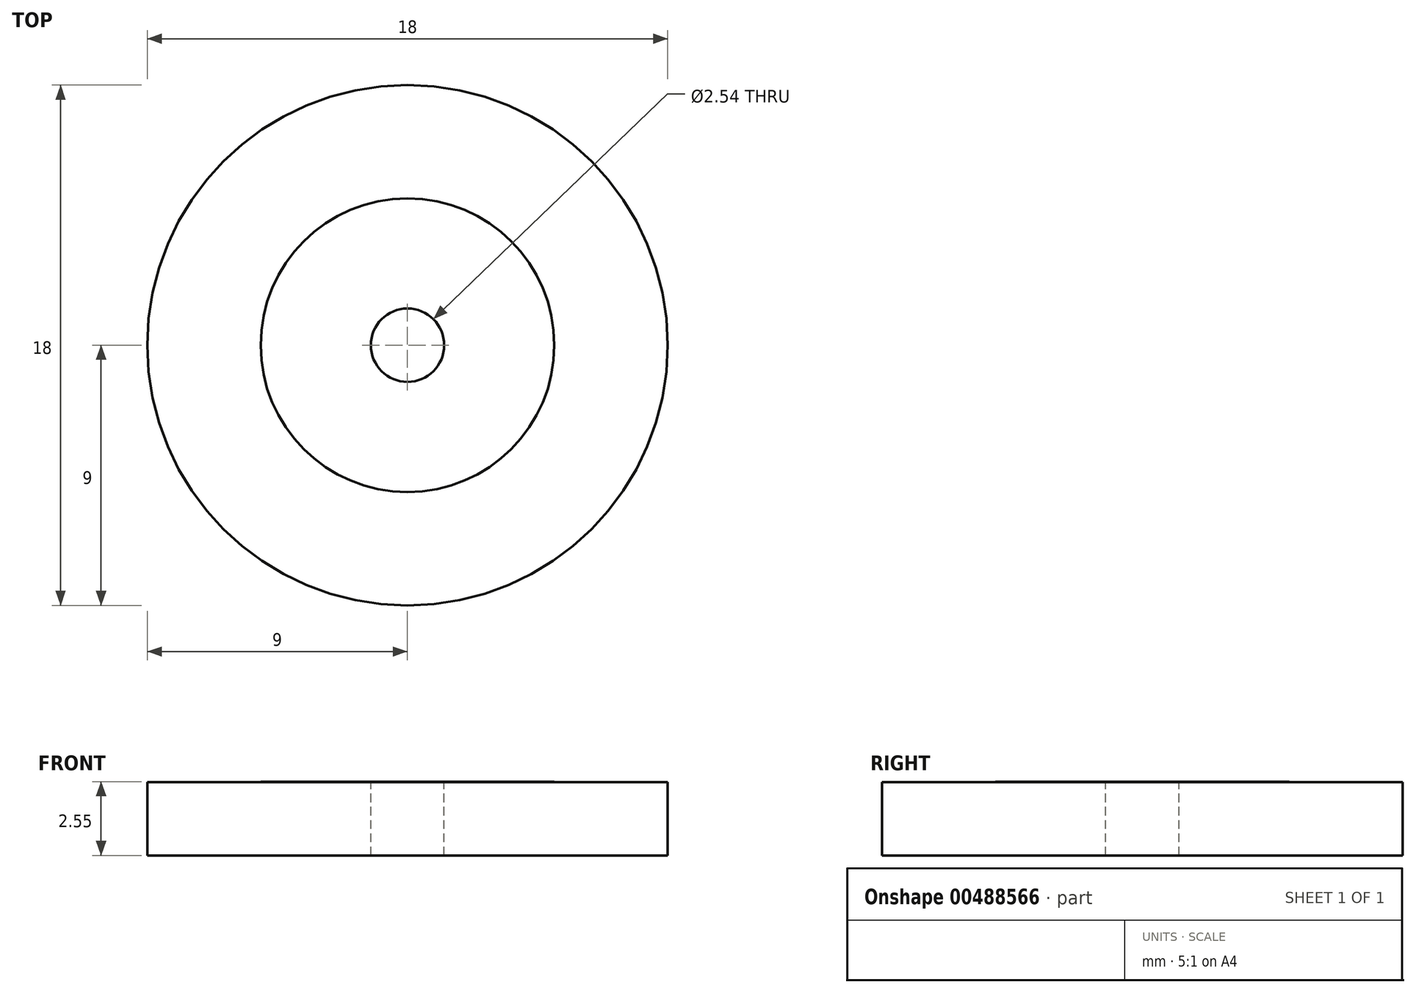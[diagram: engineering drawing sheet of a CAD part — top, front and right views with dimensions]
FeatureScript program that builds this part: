
annotation { "Feature Type Name" : "Feature", "Feature Type Description" : "" }
export const myFeature = defineFeature(function(context is Context, id is Id, definition is map)
    precondition{}
    {
        {
            var Q0;
            Q0=qCreatedBy(makeId("Top.planeOp"),FACE);
            var sketch = newSketch(context, id + "F0", { "sketchPlane" : qUnion([Q0])});
            skCircle(sketch, "E0", {"center": v(0, 0) * mm, "radius": 9 * mm});
            skSolve(sketch);
        }
        {
            var Q0;
            Q0=makeQuery(id+"F0.imprint","IMPRINT",FACE,{"disambiguationData":[TD([[makeQuery(id+"F0.imprint","IMPRINT",EDGE,{"derivedFrom":sQuery(id+"F0.wireOp",EDGE,"E0")}),1.0]])]});
            extrude(context, id + "F1", {"entities" : qUnion([Q0]), "depth" : 2.54 * mm});
        }
        {
            var Q0;
            Q0=makeQuery(id+"F1.opExtrude","CAP_FACE",FACE,{"disambiguationData":[OSD([sQuery(id+"F0.wireOp",EDGE,"E0")])],"isStart":false});
            var sketch = newSketch(context, id + "F2", { "sketchPlane" : qUnion([Q0])});
            skCircle(sketch, "E1", {"center": v(0, 0) * mm, "radius": 5.08 * mm});
            skSolve(sketch);
        }
        {
            var Q0;
            Q0 = qSketchRegion(id + "F2", true);
            extrude(context, id + "F3", {"entities" : qUnion([Q0]), "operationType" : NewBodyOperationType.ADD, "depth" : 1 / 177.8 * mm});
        }
        {
            var Q0;
            Q0=makeQuery(id+"F3.opExtrude","CAP_FACE",FACE,{"disambiguationData":[OSD([sQuery(id+"F2.wireOp",EDGE,"E1")])],"isStart":false});
            var sketch = newSketch(context, id + "F4", { "sketchPlane" : qUnion([Q0])});
            skCircle(sketch, "E2", {"center": v(0, 0) * mm, "radius": 1.27 * mm});
            skSolve(sketch);
        }
        {
            var Q0;
            Q0=makeQuery(id+"F4.imprint","IMPRINT",FACE,{"disambiguationData":[TD([[makeQuery(id+"F4.imprint","IMPRINT",EDGE,{"derivedFrom":sQuery(id+"F4.wireOp",EDGE,"E2")}),1.0]])]});
            extrude(context, id + "F5", {"entities" : qUnion([Q0]), "operationType" : NewBodyOperationType.REMOVE, "oppositeDirection" : true, "depth" : 3.63 * mm});
        }
    });
